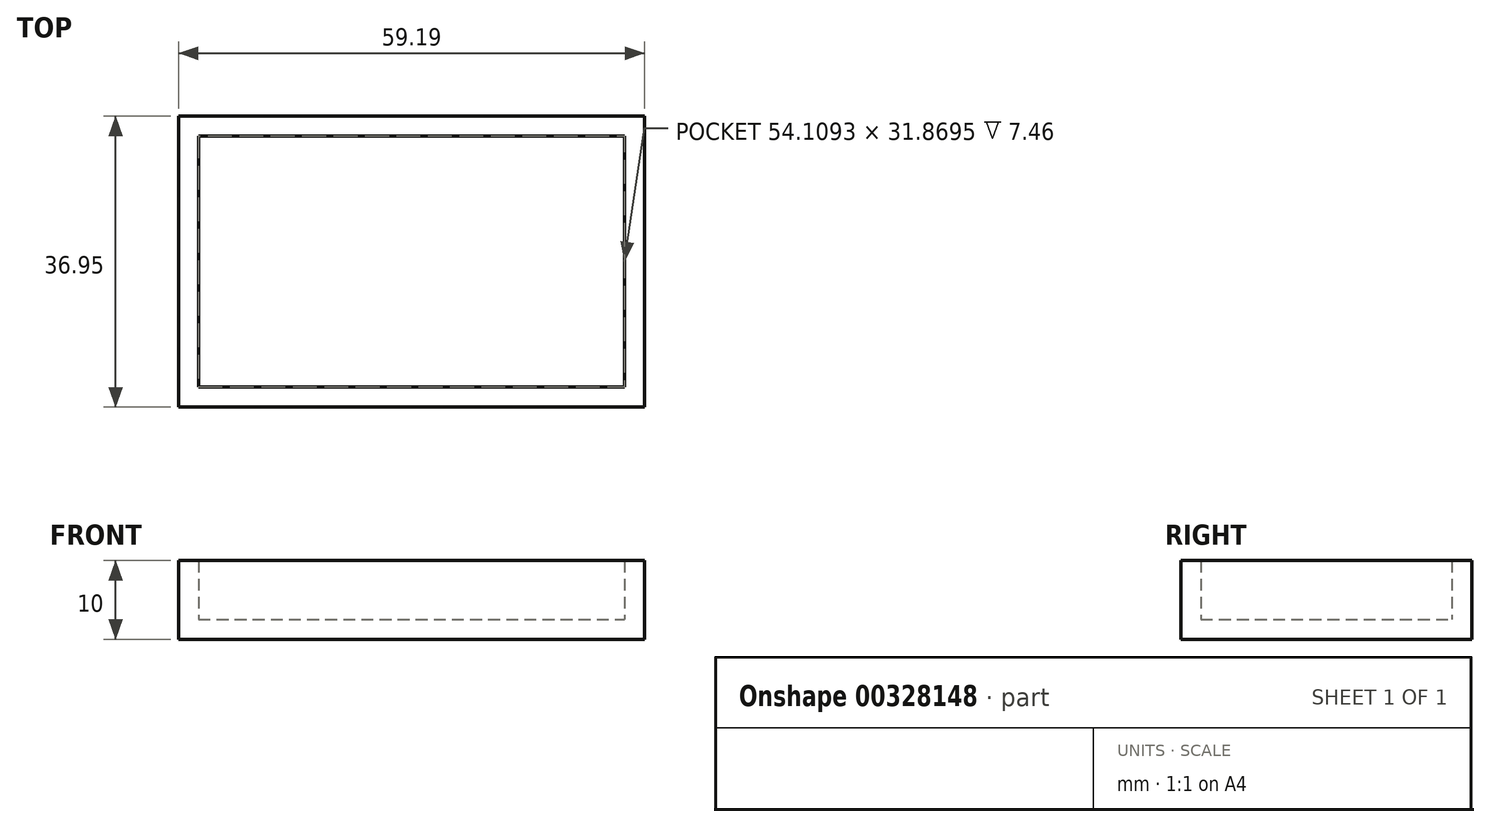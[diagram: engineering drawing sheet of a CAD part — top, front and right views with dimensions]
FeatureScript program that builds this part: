
annotation { "Feature Type Name" : "Feature", "Feature Type Description" : "" }
export const myFeature = defineFeature(function(context is Context, id is Id, definition is map)
    precondition{}
    {
        {
            var Q0;
            Q0=qCreatedBy(makeId("Top.planeOp"),FACE);
            var sketch = newSketch(context, id + "F0", { "sketchPlane" : qUnion([Q0])});
            skLineSegment(sketch, "E0.bottom", {"start": v(-25.54, -18.68) * mm, "end": v(33.65, -18.68) * mm});
            skLineSegment(sketch, "E0.top", {"start": v(-25.54, 18.27) * mm, "end": v(33.65, 18.27) * mm});
            skLineSegment(sketch, "E0.left", {"start": v(-25.54, -18.68) * mm, "end": v(-25.54, 18.27) * mm});
            skLineSegment(sketch, "E0.right", {"start": v(33.65, -18.68) * mm, "end": v(33.65, 18.27) * mm});
            skArc(sketch, "E1", {"start": v(-56.01, 11.45) * mm, "mid": v(-49.7, 15.28) * mm, "end": v(-48.51, 22.57) * mm});
            skSolve(sketch);
        }
        {
            var Q0;
            Q0 = qSketchRegion(id + "F0", true);
            extrude(context, id + "F1", {"entities" : qUnion([Q0]), "depth" : 10 * mm});
        }
        {
            var Q0;
            Q0=makeQuery(id+"F1.opExtrude","CAP_FACE",FACE,{"disambiguationData":[OSD([sQuery(id+"F0.wireOp",EDGE,"E0.bottom"),sQuery(id+"F0.wireOp",EDGE,"E0.top"),sQuery(id+"F0.wireOp",EDGE,"E0.left"),sQuery(id+"F0.wireOp",EDGE,"E0.right")])],"isStart":false});
            shell(context, id + "F2", {"entities" : qUnion([Q0]), "thickness" : 2.54 * mm});
        }
        {
            var Q0;
            Q0=sQuery(id+"F0.wireOp",EDGE,"E1");
            extrude(context, id + "F3", {"bodyType" : ToolBodyType.SURFACE, "surfaceEntities" : qUnion([Q0]), "depth" : 25.4 * mm});
        }
    });
